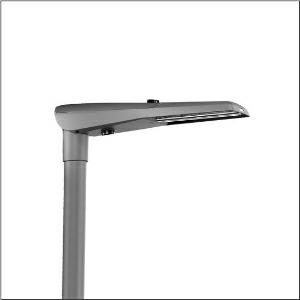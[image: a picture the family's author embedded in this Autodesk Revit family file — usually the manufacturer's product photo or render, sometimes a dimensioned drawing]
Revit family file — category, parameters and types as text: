
# Revit family: streetlight_sl_11_iq_mini___st1_2a_5xc2ac1y08ge_2c74
name_source: partatom
category: Lighting Fixtures
units: mm (PartAtom-declared; Revit-internal decimal feet)

## family parameters
Cut with Voids When Loaded = No
Host = Face
Light Source = No
Part Type = Normal
Room Calculation Point = No
Round Connector Dimension = Use Diameter
Shared = No

## types (1)
- --- (1 x LED, 3040 lm, 25.3 W, 2200K)
    Apparent Load = 25 VA
    CIE Flux Codes = 32 70 96 100 100
    Color Rendering = 70
    Color Temperature = 2200K
    Default Elevation = 1800 mm
    Description = Streetlight SL 11 iQ mini, mast luminaire, primary light control with 3 zone facetted reflector, of plastic, silver coated, highly specular, primary optical cover: cover, of PMMA, transparent, light distribution: ST1.2a, light emission: direct distribution, primary light characteristic: asymmetric, installation type: post-top, side-entry, lamps: LED, High Power LED, rated values: 3.570lm | 24,9W | 143,4lm/W (begin service life); end service life: 3.570lm | 25,7W; at 50% lumin. flux: 1.785lm | 12,8W | 139,5lm/W, colour temperature: 2200/2700/3000/4000K, colour rendering: CRI > 70, light colour: 722/727/730/740, light setting 1 begin service life: 100% | 3.570lm | 24,9W | 143,4lm/W | 3.000K, light setting 1 end service life: 25,7W, further light settings possible, control: pre-setting: logarithmic dimming characteristic, Street-Remote, Auto-Match, Temp-Guard, Lumen-Switch, Night-Set, Smart-Wire, Light-Fading, Desk-Remote (wireless, voltage-free reading and setting of iQ features in the workshop via application-optimized NFC function/RFID function), optimised constant luminous flux control (CLO 2.0), with cable H07RN-F 5x 1.5mm², mains connection: 230..240V, AC, 50/60Hz, connection cable pre-assembled, cable length: 6,5m, luminaire housing, of diecast aluminium, powder-coated, Siteco® metallic grey (DB 702S), please order mast flange separately, inclination adjustable without tools: 0°, 5°, 10°, 15° (post-top) | 0°, -5°, -10°, -15° (side-entry), sealing non-destructively replaceable, multi-level sealing system, length: 736mm, width: 174mm, height: 116mm, mast flange for spigot size: 42mm (side-entry): 5XC10008XM4, 60/48mm (side-entry/post-top): 5XC10108XM2, 76/60mm (side-entry/post-top): 5XC10108XM1, equipment: standard, Smart Interface below and above, protection rating (complete): IP66, insulation class (complete): insulation class II (safety insulation), certification: CE, ENEC, ENEC+, VDE, UKCA, impact resistance: IK10, permissible operating ambient temperature for outdoor applications: -25..+50°C, standard-compliant lighting for roads and squares, Environmental Product Declaration (EPD) tested and certified by an independent institute, packaging unit: 1 piece

Light Distribution: ST1.2a
    Height = 116 mm
    Lamp = 1 x LED
    Lamp Light Flux = 3040 lm
    Lamp Power = 25.3 W
    Lamp count = 1
    Length = 736 mm
    Luminous efficacy = 120 lm/W
    Manufacturer = Siteco
    ModVariant = No
    Model = 5XC2AC1Y08GE
    Number of Poles = 1
    OnlyDefault = Yes
    Power Factor = 1
    Product Name = Streetlight SL 11 iQ mini | ST1.2a
    Product group = mast luminaire | pylon top
    ProductGroupID = 6100
    Protection Class = Protection class II
    Protection Degree = IP 66
    RLX_Detail_Level = 1
    RLX_Emergency_Light_Flux = 0 lm
    RLX_Emergency_Type = 0
    RLX_Emergency_Type_DB = No
    RlxData = <blob elided: 53697 chars, md5=2a52a8d7>
    Socket = socket
    Standby Power = 0 W
    System Light Flux = 3040 lm
    System Power = 25 W
    Type Comments = individual setting: luminous flux: 100 % | dim-lin: 254 | 351 mA
    Type Image = l_1006751.jpg
    URL = http://relux.com
    VarID = @adj_035034
    Voltage = 0 V
    Weight = 0.00 kg
    Width = 174 mm

## geometry (parser evidence)
native form markers: Blend x4, Sweep x11
no freeform markers — native parametric forms only
